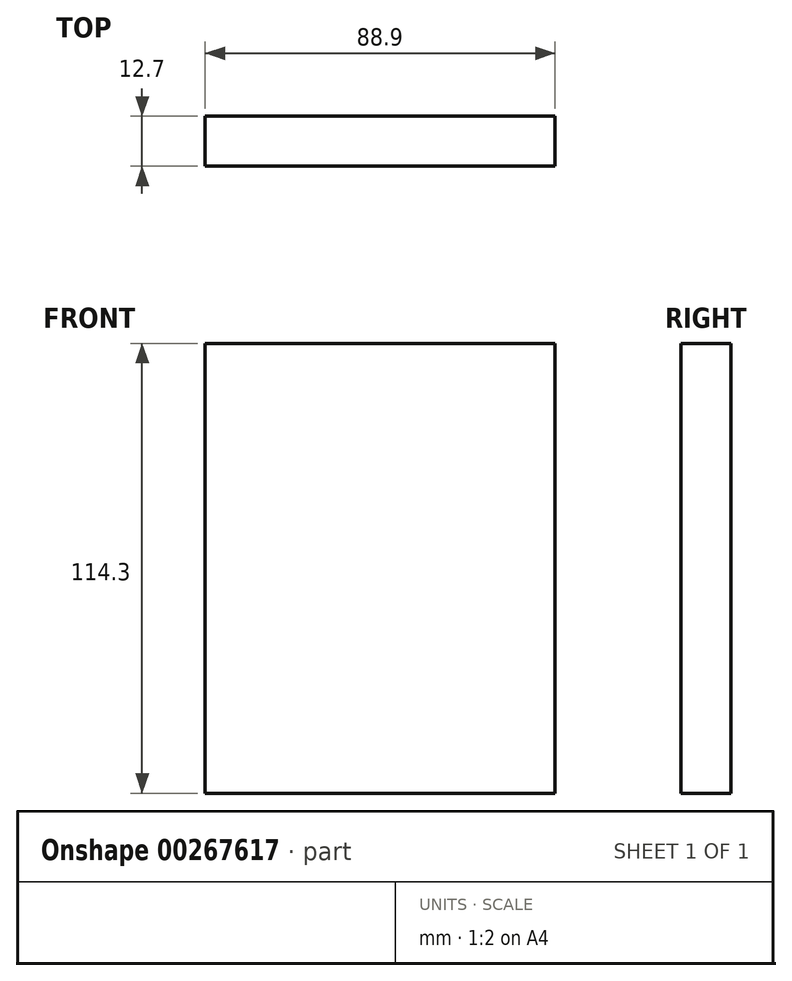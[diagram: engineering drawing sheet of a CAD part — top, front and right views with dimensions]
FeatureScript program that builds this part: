
annotation { "Feature Type Name" : "Feature", "Feature Type Description" : "" }
export const myFeature = defineFeature(function(context is Context, id is Id, definition is map)
    precondition{}
    {
        {
            var Q0;
            Q0=qCreatedBy(makeId("Front.planeOp"),FACE);
            var sketch = newSketch(context, id + "F0", { "sketchPlane" : qUnion([Q0])});
            skLineSegment(sketch, "E0.bottom", {"start": v(44.45, 57.15) * mm, "end": v(-44.45, 57.15) * mm});
            skLineSegment(sketch, "E0.top", {"start": v(44.45, -57.15) * mm, "end": v(-44.45, -57.15) * mm});
            skLineSegment(sketch, "E0.left", {"start": v(44.45, 57.15) * mm, "end": v(44.45, -57.15) * mm});
            skLineSegment(sketch, "E0.right", {"start": v(-44.45, 57.15) * mm, "end": v(-44.45, -57.15) * mm});
            skPoint(sketch, "E0.middle", {"position": v(0, 0) * mm});
            skSolve(sketch);
        }
        {
            var Q0;
            Q0 = qSketchRegion(id + "F0", true);
            extrude(context, id + "F1", {"entities" : qUnion([Q0]), "depth" : 12.7 * mm});
        }
    });
